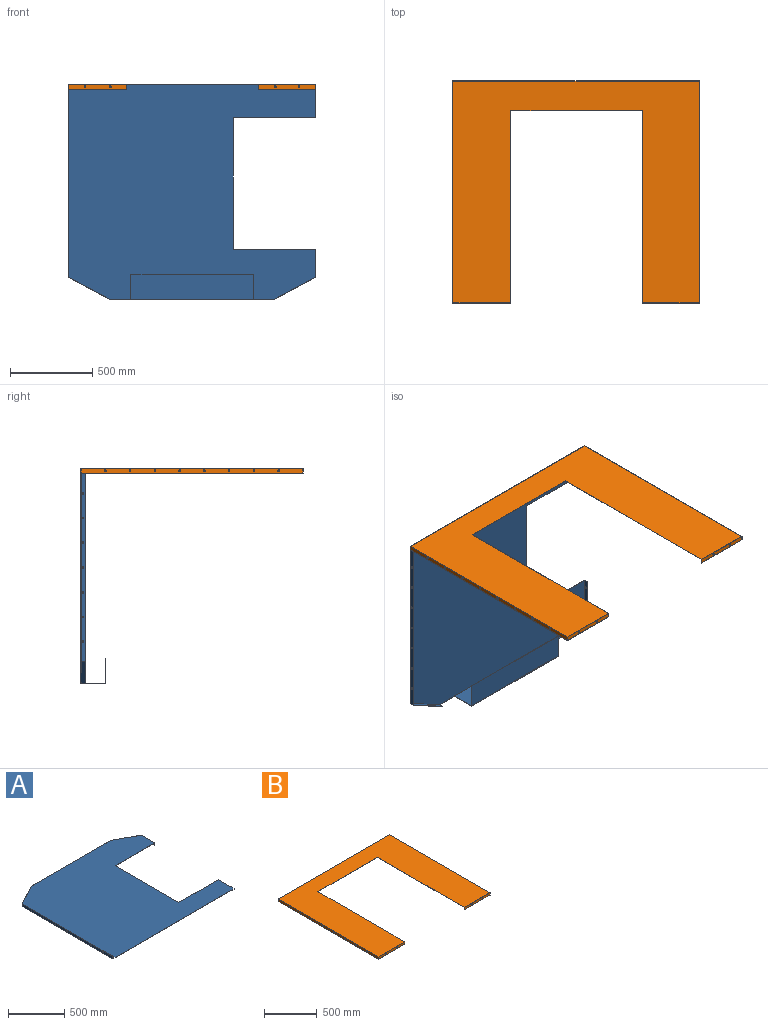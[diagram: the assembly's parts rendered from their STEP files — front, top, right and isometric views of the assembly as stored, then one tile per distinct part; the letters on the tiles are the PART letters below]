
ASSEMBLY  parts=2 mates=1
PART A: 43 faces, bbox 1497x1300.5x151 mm
  f0: plane 742.17x148mm, normal (0,0,1), area 109841.3mm2, adj f1,f2,f3,f4
  f1: plane 150x149mm, normal (1,0,0), area 594mm2, adj f0,f2,f4,f5,f21,f33
  f2: plane 742.17x2mm, normal (0,-1,0), area 1484.3mm2, adj f0,f1,f3,f21
  f3: plane 150x149mm, normal (-1,0,0), area 594mm2, adj f0,f2,f4,f5,f21,f33
  f4: plane 742.17x147mm, normal (0,-1,0), area 109099.1mm2, adj f0,f1,f3,f5
  f5: plane 1493x1300.5mm, normal (0,0,-1), area 1509337.6mm2, adj f1,f3,f4,f6,f7,f8,f10,f14
  f6: plane 25x2mm, normal (-1,0,0), area 50mm2, adj f5,f7,f9,f33
  f7: plane 25x3.75mm, normal (0,-1,0), area 93.7mm2, adj f5,f6,f8,f9
  f8: plane 248.79x132.7mm, normal (-0.47,-0.88,0), area 7049.2mm2, adj f5,f7,f9,f10
  f9: plane 302.5x254.54mm, normal (0,0,-1), area 910.4mm2, adj f6,f7,f8,f10,f12,f18,f22,f33
  f10: plane 167.8x25mm, normal (-1,0,0), area 4116.5mm2, adj f5,f8,f9,f11,f18
  f11: cylinder r=5mm len=10mm, axis (1,0,0), area 62.8mm2, adj f10,f12
  f12: plane 169x27mm, normal (1,0,0), area 4484.5mm2, adj f9,f11,f18,f22,f39
  f13: plane 27x2mm, normal (0,-1,0), area 54mm2, adj f14,f17,f20,f39,f41
  f14: plane 173x25mm, normal (-1,0,0), area 4246.5mm2, adj f5,f13,f15,f16,f17
  f15: cylinder r=5mm len=10mm, axis (1,0,0), area 62.8mm2, adj f14,f20
  f16: plane 498x27mm, normal (0,1,0), area 1046mm2, adj f5,f14,f17,f19,f20,f39
  f17: plane 173x2mm, normal (0,0,-1), area 346mm2, adj f13,f14,f16,f20
  f18: plane 498x27mm, normal (0,-1,0), area 1046mm2, adj f5,f9,f10,f12,f19,f39
  f19: plane 800x2mm, normal (1,0,0), area 1600mm2, adj f5,f16,f18,f39
  f20: plane 173x27mm, normal (1,0,0), area 4592.5mm2, adj f13,f15,f16,f17,f39
  f21: plane 742.17x150mm, normal (0,0,-1), area 111325.6mm2, adj f1,f2,f3,f33
  f22: plane 250.29x133.5mm, normal (0.47,0.88,0), area 7659mm2, adj f9,f12,f33,f39
  f23: plane 27x2mm, normal (0,-1,0), area 54mm2, adj f34,f35,f38,f39,f42
  f24: cylinder r=5mm len=10mm, axis (1,0,0), area 62.8mm2, adj f34,f35
  f25: cylinder r=5mm len=10mm, axis (1,0,0), area 62.8mm2, adj f34,f35
  f26: cylinder r=5mm len=10mm, axis (1,0,0), area 62.8mm2, adj f34,f35
  f27: cylinder r=5mm len=10mm, axis (1,0,0), area 62.8mm2, adj f34,f35
  f28: cylinder r=5mm len=10mm, axis (1,0,0), area 62.8mm2, adj f34,f35
  f29: cylinder r=5mm len=10mm, axis (1,0,0), area 62.8mm2, adj f34,f35
  f30: cylinder r=5mm len=10mm, axis (1,0,0), area 62.8mm2, adj f34,f35
  f31: plane 25x2mm, normal (1,0,0), area 50mm2, adj f5,f32,f33,f38
  f32: plane 25x3.75mm, normal (0,-1,0), area 93.7mm2, adj f5,f31,f36,f38
  f33: plane 996.42x151mm, normal (0,1,0), area 112788.8mm2, adj f1,f3,f5,f6,f9,f21,f22,f31
  f34: plane 1140.8x25mm, normal (1,0,0), area 27970.2mm2, adj f5,f23,f24,f25,f26,f27,f28,f29
  f35: plane 1142x27mm, normal (-1,0,0), area 30284.2mm2, adj f23,f24,f25,f26,f27,f28,f29,f30
  f36: plane 248.79x132.7mm, normal (0.47,-0.88,0), area 7049.2mm2, adj f5,f32,f34,f38
  f37: plane 250.29x133.5mm, normal (-0.47,0.88,0), area 7659mm2, adj f33,f35,f38,f39
  f38: plane 1275.5x254.54mm, normal (0,0,-1), area 2856.4mm2, adj f23,f31,f32,f33,f34,f35,f36,f37
  f39: plane 1497x1300.5mm, normal (0,0,1), area 1514934.8mm2, adj f12,f13,f16,f18,f19,f20,f22,f23
  f40: plane 1493x2mm, normal (0,-1,0), area 2986mm2, adj f5,f39,f41,f42
  f41: plane 25x2mm, normal (1,0,0), area 50mm2, adj f5,f13,f39,f40
  f42: plane 25x2mm, normal (-1,0,0), area 50mm2, adj f5,f23,f39,f40
PART B: 48 faces, bbox 1497x1350x27 mm
  f0: cylinder r=5mm len=5mm, axis (0,-1,0), area 15.7mm2, adj f1,f2,f42,f43
  f1: cylinder r=5mm len=5mm, axis (0,-1,0), area 15.7mm2, adj f0,f9,f42,f43
  f2: cylinder r=5mm len=5mm, axis (0,-1,0), area 15.7mm2, adj f0,f9,f42,f43
  f3: plane 1350x27mm, normal (-1,0,0), area 35821.7mm2, adj f4,f12,f13,f14,f15,f16,f17,f18
  f4: plane 1497x1350mm, normal (0,0,1), area 1086549.9mm2, adj f3,f12,f21,f22,f23,f24,f42,f46
  f5: cylinder r=5mm len=5mm, axis (0,-1,0), area 15.7mm2, adj f6,f8,f42,f43
  f6: cylinder r=5mm len=5mm, axis (0,-1,0), area 15.7mm2, adj f5,f7,f42,f43
  f7: cylinder r=5mm len=5mm, axis (0,-1,0), area 15.7mm2, adj f6,f8,f42,f43
  f8: cylinder r=5mm len=5mm, axis (0,-1,0), area 15.7mm2, adj f5,f7,f42,f43
  f9: cylinder r=5mm len=5mm, axis (0,-1,0), area 15.7mm2, adj f1,f2,f42,f43
  f10: plane 1348x25mm, normal (1,0,0), area 33071.7mm2, adj f11,f12,f13,f14,f15,f16,f17,f18
  f11: plane 1493x1348mm, normal (0,0,-1), area 1079763.9mm2, adj f10,f12,f21,f22,f24,f25,f43,f47
  f12: plane 1497x27mm, normal (0,1,0), area 3094mm2, adj f3,f4,f10,f11,f23,f25,f44,f45
  f13: cylinder r=5mm len=10mm, axis (1,0,0), area 62.8mm2, adj f3,f10
  f14: cylinder r=5mm len=10mm, axis (1,0,0), area 62.8mm2, adj f3,f10
  f15: cylinder r=5mm len=10mm, axis (1,0,0), area 62.8mm2, adj f3,f10
  f16: cylinder r=5mm len=10mm, axis (1,0,0), area 62.8mm2, adj f3,f10
  f17: cylinder r=5mm len=10mm, axis (1,0,0), area 62.8mm2, adj f3,f10
  f18: cylinder r=5mm len=10mm, axis (1,0,0), area 62.8mm2, adj f3,f10
  f19: cylinder r=5mm len=10mm, axis (1,0,0), area 62.8mm2, adj f3,f10
  f20: cylinder r=5mm len=10mm, axis (1,0,0), area 62.8mm2, adj f3,f10
  f21: plane 800x2mm, normal (0,-1,0), area 1600mm2, adj f4,f11,f22,f24
  f22: plane 1168x27mm, normal (-1,0,0), area 2386mm2, adj f4,f11,f21,f45,f46,f47
  f23: plane 1350x27mm, normal (1,0,0), area 35821.7mm2, adj f4,f12,f34,f35,f36,f37,f38,f39
  f24: plane 1168x27mm, normal (1,0,0), area 2386mm2, adj f4,f11,f21,f42,f43,f44
  f25: plane 1348x25mm, normal (-1,0,0), area 33071.7mm2, adj f11,f12,f34,f35,f36,f37,f38,f39
  f26: cylinder r=5mm len=5mm, axis (0,-1,0), area 15.7mm2, adj f27,f29,f46,f47
  f27: cylinder r=5mm len=5mm, axis (0,-1,0), area 15.7mm2, adj f26,f28,f46,f47
  f28: cylinder r=5mm len=5mm, axis (0,-1,0), area 15.7mm2, adj f27,f29,f46,f47
  f29: cylinder r=5mm len=5mm, axis (0,-1,0), area 15.7mm2, adj f26,f28,f46,f47
  f30: cylinder r=5mm len=5mm, axis (0,-1,0), area 15.7mm2, adj f31,f33,f46,f47
  f31: cylinder r=5mm len=5mm, axis (0,-1,0), area 15.7mm2, adj f30,f32,f46,f47
  f32: cylinder r=5mm len=5mm, axis (0,-1,0), area 15.7mm2, adj f31,f33,f46,f47
  f33: cylinder r=5mm len=5mm, axis (0,-1,0), area 15.7mm2, adj f30,f32,f46,f47
  f34: cylinder r=5mm len=10mm, axis (1,0,0), area 62.8mm2, adj f23,f25
  f35: cylinder r=5mm len=10mm, axis (1,0,0), area 62.8mm2, adj f23,f25
  f36: cylinder r=5mm len=10mm, axis (1,0,0), area 62.8mm2, adj f23,f25
  f37: cylinder r=5mm len=10mm, axis (1,0,0), area 62.8mm2, adj f23,f25
  f38: cylinder r=5mm len=10mm, axis (1,0,0), area 62.8mm2, adj f23,f25
  f39: cylinder r=5mm len=10mm, axis (1,0,0), area 62.8mm2, adj f23,f25
  f40: cylinder r=5mm len=10mm, axis (1,0,0), area 62.8mm2, adj f23,f25
  f41: cylinder r=5mm len=10mm, axis (1,0,0), area 62.8mm2, adj f23,f25
  f42: plane 353.5x27mm, normal (0,-1,0), area 9387.5mm2, adj f0,f1,f2,f3,f4,f5,f6,f7
  f43: plane 351.5x25mm, normal (0,1,0), area 8630.5mm2, adj f0,f1,f2,f5,f6,f7,f8,f9
  f44: plane 1350x353.5mm, normal (0,0,-1), area 3403mm2, adj f3,f10,f12,f24,f42,f43
  f45: plane 1350x343.5mm, normal (0,0,-1), area 3383mm2, adj f12,f22,f23,f25,f46,f47
  f46: plane 343.5x27mm, normal (0,-1,0), area 9117.4mm2, adj f4,f22,f23,f26,f27,f28,f29,f30
  f47: plane 341.5x25mm, normal (0,1,0), area 8380.4mm2, adj f11,f22,f25,f26,f27,f28,f29,f30
PLACE A rot(axis=(-1,0,0),90deg) t=(-445.72,-95.69,621.53)mm
PLACE B t=(-445.72,-95.69,621.53)mm fixed
MATE fastened A.f40 <-> B.f11  axis (0,0,1) through (-441.72,1256.31,619.53)mm
